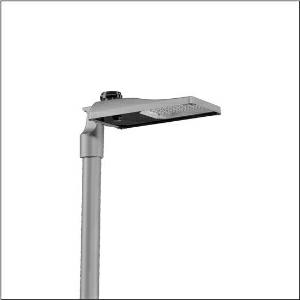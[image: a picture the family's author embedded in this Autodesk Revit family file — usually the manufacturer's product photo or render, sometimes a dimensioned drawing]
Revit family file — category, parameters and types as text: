
# Revit family: streetlight_sl_31_mini___st1_0a_5xh6d35m08ja_363a
name_source: partatom
category: Lighting Fixtures
units: mm (PartAtom-declared; Revit-internal decimal feet)

## family parameters
Cut with Voids When Loaded = No
Host = Face
Light Source = No
Part Type = Normal
Room Calculation Point = No
Round Connector Dimension = Use Diameter
Shared = No

## types (1)
- --- (1 x LED, 12270 lm, 82.5 W, 3000K)
    Apparent Load = 83 VA
    CIE Flux Codes = 40 73 97 100 100
    Color Rendering = 70
    Color Temperature = 3000K
    Default Elevation = 1800 mm
    Description = Streetlight SL 31 mini NEMA (7pin), Desk-Remote mast luminaire for post-top, side-entry; light control with lens of PMMA; light distribution: ST1.0a, direct asymmetric distribution, for standard-compliant lighting for roads and squares; LED: luminous flux: 12.270lm, light colour: 730, colour temperature: 3000K; luminous efficacy: 148,7lm/W; control: pre-setting: linear dimming characteristic, flexible luminous flux parameterisation, time-dependent luminous flux control, constant luminous flux control, intelligent temperature release in ECG and LED module, overheat protection; luminaire housing, of diecast aluminium, SITECO metallic grey (DB 702S), corrosivity category C5 high according to DIN EN ISO 12944; cover of toughened safety glass, transparent, opened without tools; mast flange of diecast aluminium, SITECO metallic grey (DB 702S), spigot size: 76/60mm, mast flange included unmounted; cable length: 10,5m, connection cable pre-assembled; mains connection: 220..240V, AC, 50/60Hz; power consumption (at start of service life): 82,5W / (at end of service life): 90,1W / (with reduced operation 50%): 36,8W; protection rating (complete): IP66; insulation class (complete): insulation class I (protective earthing); impact resistance: IK09; certification: CE, ENEC, ENEC+, VDE, UKCA; permissible operating ambient temperature for outdoor applications: -40..+50°C; packaging unit: 1 piece

Light Distribution: ST1.0a
    Height = 76 mm
    Lamp = 1 x LED
    Lamp Light Flux = 12270 lm
    Lamp Power = 82.5 W
    Lamp count = 1
    Length = 547 mm
    Luminous efficacy = 149 lm/W
    Manufacturer = Siteco
    ModVariant = No
    Model = 5XH6D35M08JA
    Number of Poles = 1
    OnlyDefault = Yes
    Power Factor = 1
    Product Name = Streetlight SL 31 mini | ST1.0a
    Product group = mast luminaire | pylon top
    ProductGroupID = 6100
    Protection Class = Protection class I
    Protection Degree = IP 66
    RLX_Detail_Level = 1
    RLX_Emergency_Light_Flux = 0 lm
    RLX_Emergency_Type = 0
    RLX_Emergency_Type_DB = No
    RlxData = <blob elided: 40293 chars, md5=2cdc34bd>
    Socket = socket
    Standby Power = 0 W
    System Light Flux = 12270 lm
    System Power = 83 W
    Type Comments = factory setting: luminous flux: 100 % | dim-lin: 254 | 870 mA
    Type Image = l_1300324.jpg
    URL = http://relux.com
    VarID = @adj_056915
    Voltage = 0 V
    Weight = 0.00 kg
    Width = 265 mm

## geometry (parser evidence)
native form markers: Blend x4, Sweep x9
no freeform markers — native parametric forms only
